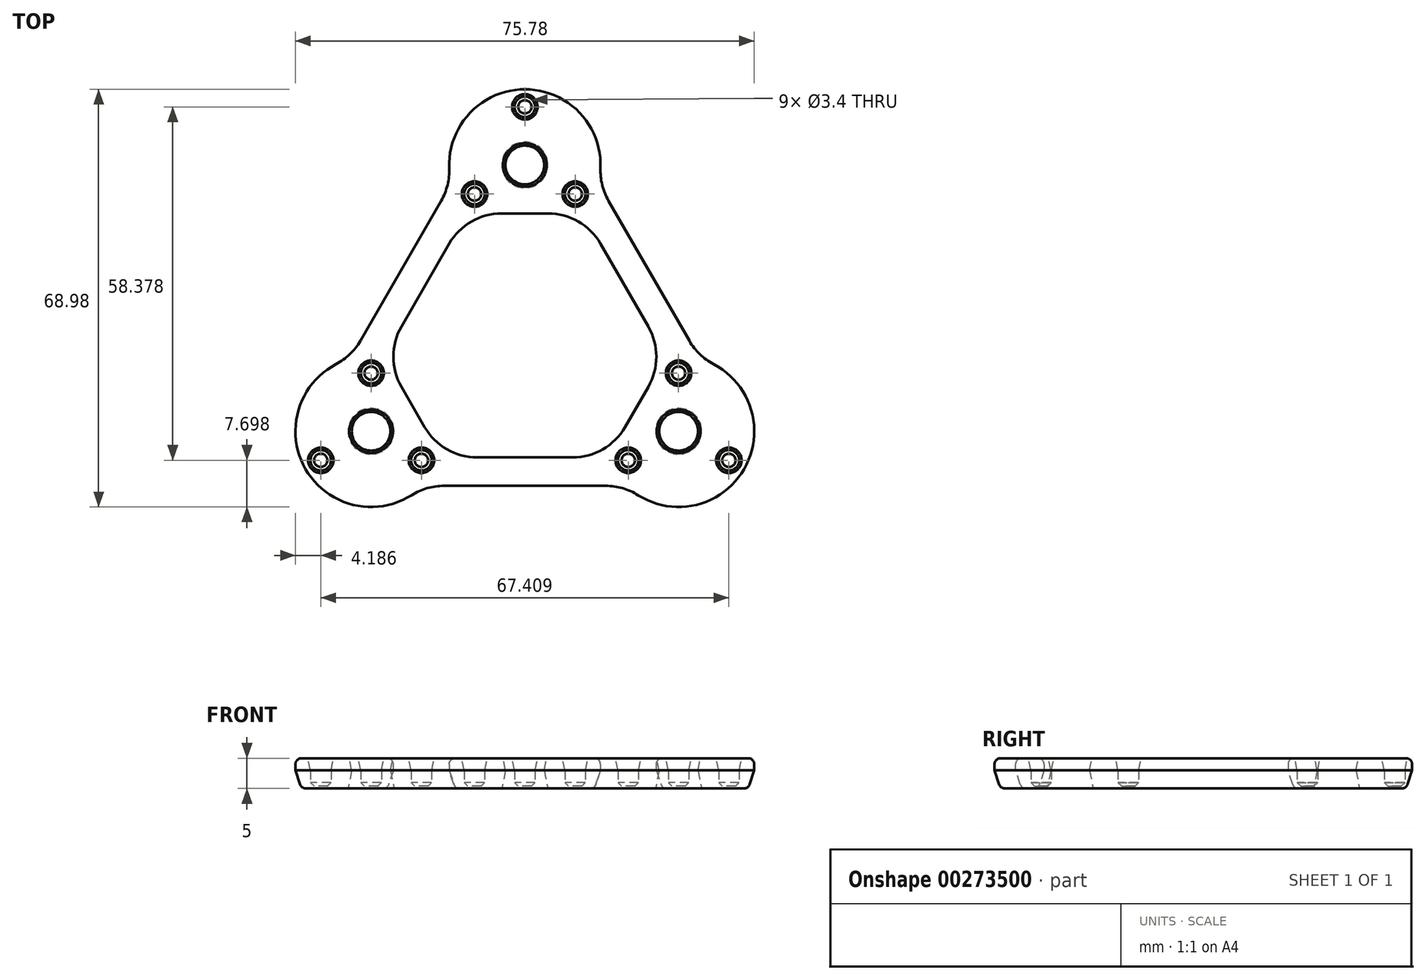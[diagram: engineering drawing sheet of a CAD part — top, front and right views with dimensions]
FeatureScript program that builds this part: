
annotation { "Feature Type Name" : "Feature", "Feature Type Description" : "" }
export const myFeature = defineFeature(function(context is Context, id is Id, definition is map)
    precondition{}
    {
        {
            var Q0;
            Q0=qCreatedBy(makeId("Top.planeOp"),FACE);
            var sketch = newSketch(context, id + "F0", { "sketchPlane" : qUnion([Q0])});
            skCircle(sketch, "E0", {"center": v(0, 29.45) * mm, "radius": 3.2 * mm});
            skCircle(sketch, "E1", {"center": v(0, 29.45) * mm, "radius": 12.5 * mm});
            skCircle(sketch, "E2", {"center": v(0, 39.05) * mm, "radius": 1.7 * mm});
            skCircle(sketch, "E3.1.0", {"center": v(-8.31, 24.65) * mm, "radius": 1.7 * mm});
            skCircle(sketch, "E3.2.0", {"center": v(8.31, 24.65) * mm, "radius": 1.7 * mm});
            skLineSegment(sketch, "E4", {"start": v(-9.6, 21.45) * mm, "end": v(9.6, 21.45) * mm});
            skLineSegment(sketch, "E5", {"start": v(12.13, 26.45) * mm, "end": v(-12.13, 26.45) * mm, "construction": true});
            skCircle(sketch, "E6.1.0", {"center": v(-25.4, -14.53) * mm, "radius": 12.5 * mm});
            skCircle(sketch, "E6.1.1", {"center": v(-17.08, -19.33) * mm, "radius": 1.7 * mm});
            skLineSegment(sketch, "E6.1.2", {"start": v(-13.66, -18.85) * mm, "end": v(-23.26, -2.21) * mm});
            skCircle(sketch, "E6.1.3", {"center": v(-25.4, -4.93) * mm, "radius": 1.7 * mm});
            skPoint(sketch, "E6.1.4", {"position": v(-25.4, -14.53) * mm});
            skLineSegment(sketch, "E6.1.5", {"start": v(-28.86, -2.52) * mm, "end": v(-16.73, -23.54) * mm, "construction": true});
            skCircle(sketch, "E6.1.6", {"center": v(-25.4, -14.53) * mm, "radius": 3.2 * mm});
            skCircle(sketch, "E6.1.7", {"center": v(-33.7, -19.33) * mm, "radius": 1.7 * mm});
            skCircle(sketch, "E6.2.0", {"center": v(25.4, -14.53) * mm, "radius": 12.5 * mm});
            skCircle(sketch, "E6.2.1", {"center": v(25.4, -4.93) * mm, "radius": 1.7 * mm});
            skLineSegment(sketch, "E6.2.2", {"start": v(23.26, -2.21) * mm, "end": v(13.66, -18.85) * mm});
            skCircle(sketch, "E6.2.3", {"center": v(17.08, -19.33) * mm, "radius": 1.7 * mm});
            skPoint(sketch, "E6.2.4", {"position": v(25.4, -14.53) * mm});
            skLineSegment(sketch, "E6.2.5", {"start": v(16.73, -23.54) * mm, "end": v(28.86, -2.52) * mm, "construction": true});
            skCircle(sketch, "E6.2.6", {"center": v(25.4, -14.53) * mm, "radius": 3.2 * mm});
            skCircle(sketch, "E6.2.7", {"center": v(33.7, -19.33) * mm, "radius": 1.7 * mm});
            skPoint(sketch, "E6.center", {"position": v(0, 0.13) * mm});
            skLineSegment(sketch, "E7", {"start": v(-23.26, -2.21) * mm, "end": v(-9.6, 21.45) * mm});
            skLineSegment(sketch, "E8", {"start": v(9.6, 21.45) * mm, "end": v(23.26, -2.21) * mm});
            skLineSegment(sketch, "E9", {"start": v(13.66, -18.85) * mm, "end": v(-13.66, -18.85) * mm});
            skLineSegment(sketch, "E10", {"start": v(-28.86, -2.52) * mm, "end": v(-12.13, 26.45) * mm});
            skLineSegment(sketch, "E11", {"start": v(12.13, 26.45) * mm, "end": v(28.86, -2.52) * mm});
            skLineSegment(sketch, "E12", {"start": v(-16.73, -23.54) * mm, "end": v(16.73, -23.54) * mm});
            skSolve(sketch);
        }
        {
            var Q0;
            Q0 = qSketchRegion(id + "F0", true);
            extrude(context, id + "F1", {"entities" : qUnion([Q0]), "depth" : 5 * mm, "offsetDistance" : 25 * mm});
        }
        {
            var Q0;
            Q0=makeQuery(id+"F0.imprint","IMPRINT",FACE,{"disambiguationData":[TD([[makeQuery(id+"F0.imprint","IMPRINT",EDGE,{"derivedFrom":sQuery(id+"F0.wireOp",EDGE,"E6.2.7")}),1.0]])]});
            var Q1;
            Q1=makeQuery(id+"F0.imprint","IMPRINT",FACE,{"disambiguationData":[TD([[makeQuery(id+"F0.imprint","IMPRINT",EDGE,{"derivedFrom":sQuery(id+"F0.wireOp",EDGE,"E6.2.1")}),1.0]])]});
            var Q2;
            Q2=makeQuery(id+"F0.imprint","IMPRINT",FACE,{"disambiguationData":[TD([[makeQuery(id+"F0.imprint","IMPRINT",EDGE,{"derivedFrom":sQuery(id+"F0.wireOp",EDGE,"E2")}),1.0]])]});
            var Q3;
            Q3=makeQuery(id+"F0.imprint","IMPRINT",FACE,{"disambiguationData":[TD([[makeQuery(id+"F0.imprint","IMPRINT",EDGE,{"derivedFrom":sQuery(id+"F0.wireOp",EDGE,"E6.1.3")}),1.0]])]});
            var Q4;
            Q4=makeQuery(id+"F0.imprint","IMPRINT",FACE,{"disambiguationData":[TD([[makeQuery(id+"F0.imprint","IMPRINT",EDGE,{"derivedFrom":sQuery(id+"F0.wireOp",EDGE,"E6.1.1")}),1.0]])]});
            var Q5;
            Q5=makeQuery(id+"F0.imprint","IMPRINT",FACE,{"disambiguationData":[TD([[makeQuery(id+"F0.imprint","IMPRINT",EDGE,{"derivedFrom":sQuery(id+"F0.wireOp",EDGE,"E6.1.7")}),1.0]])]});
            var Q6;
            Q6=makeQuery(id+"F0.imprint","IMPRINT",FACE,{"disambiguationData":[TD([[makeQuery(id+"F0.imprint","IMPRINT",EDGE,{"derivedFrom":sQuery(id+"F0.wireOp",EDGE,"E6.2.3")}),1.0]])]});
            var Q7;
            Q7=makeQuery(id+"F0.imprint","IMPRINT",FACE,{"disambiguationData":[TD([[makeQuery(id+"F0.imprint","IMPRINT",EDGE,{"derivedFrom":sQuery(id+"F0.wireOp",EDGE,"E3.2.0")}),1.0]])]});
            var Q8;
            Q8=makeQuery(id+"F0.imprint","IMPRINT",FACE,{"disambiguationData":[TD([[makeQuery(id+"F0.imprint","IMPRINT",EDGE,{"derivedFrom":sQuery(id+"F0.wireOp",EDGE,"E3.1.0")}),1.0]])]});
            extrude(context, id + "F2", {"entities" : qUnion([Q0, Q1, Q2, Q3, Q4, Q5, Q6, Q7, Q8]), "operationType" : NewBodyOperationType.ADD, "depth" : 0.4 * mm, "offsetDistance" : 25 * mm});
        }
        {
            var Q0;
            Q0=makeQuery(id+"F1.opExtrude","CAP_EDGE",EDGE,{"disambiguationData":[OSD([sQuery(id+"F0.wireOp",EDGE,"E6.1.6")])],"isStart":true});
            var Q1;
            Q1=makeQuery(id+"F1.opExtrude","CAP_EDGE",EDGE,{"disambiguationData":[OSD([sQuery(id+"F0.wireOp",EDGE,"E6.2.6")])],"isStart":true});
            var Q2;
            Q2=makeQuery(id+"F1.opExtrude","CAP_EDGE",EDGE,{"disambiguationData":[OSD([sQuery(id+"F0.wireOp",EDGE,"E0")])],"isStart":true});
            chamfer(context, id + "F3", {"entities" : qUnion([Q0, Q1, Q2]), "chamferType" : ChamferType.TWO_OFFSETS, "width1" : 0.6 * mm, "oppositeDirection" : false, "width2" : 3 * mm, "tangentPropagation" : true});
        }
        {
            var Q0;
            Q0=makeQuery(id+"F1.opExtrude","SWEPT_EDGE",EDGE,{"disambiguationData":[OSD([sQuery(id+"F0.wireOp",EDGE,"E1"),sQuery(id+"F0.wireOp",EDGE,"E4"),sQuery(id+"F0.wireOp",EDGE,"E7")])]});
            var Q1;
            Q1=makeQuery(id+"F1.opExtrude","SWEPT_EDGE",EDGE,{"disambiguationData":[OSD([sQuery(id+"F0.wireOp",EDGE,"E1"),sQuery(id+"F0.wireOp",EDGE,"E4"),sQuery(id+"F0.wireOp",EDGE,"E8")])]});
            var Q2;
            Q2=makeQuery(id+"F1.opExtrude","SWEPT_EDGE",EDGE,{"disambiguationData":[OSD([sQuery(id+"F0.wireOp",EDGE,"E6.1.0"),sQuery(id+"F0.wireOp",EDGE,"E6.1.2"),sQuery(id+"F0.wireOp",EDGE,"E7")])]});
            var Q3;
            Q3=makeQuery(id+"F1.opExtrude","SWEPT_EDGE",EDGE,{"disambiguationData":[OSD([sQuery(id+"F0.wireOp",EDGE,"E6.1.0"),sQuery(id+"F0.wireOp",EDGE,"E6.1.2"),sQuery(id+"F0.wireOp",EDGE,"E9")])]});
            var Q4;
            Q4=makeQuery(id+"F1.opExtrude","SWEPT_EDGE",EDGE,{"disambiguationData":[OSD([sQuery(id+"F0.wireOp",EDGE,"E6.2.0"),sQuery(id+"F0.wireOp",EDGE,"E6.2.2"),sQuery(id+"F0.wireOp",EDGE,"E9")])]});
            var Q5;
            Q5=makeQuery(id+"F1.opExtrude","SWEPT_EDGE",EDGE,{"disambiguationData":[OSD([sQuery(id+"F0.wireOp",EDGE,"E6.2.0"),sQuery(id+"F0.wireOp",EDGE,"E6.2.2"),sQuery(id+"F0.wireOp",EDGE,"E8")])]});
            var Q6;
            Q6=makeQuery(id+"F1.opExtrude","SWEPT_EDGE",EDGE,{"disambiguationData":[OSD([sQuery(id+"F0.wireOp",EDGE,"E6.2.0"),sQuery(id+"F0.wireOp",EDGE,"E12")])]});
            var Q7;
            Q7=makeQuery(id+"F1.opExtrude","SWEPT_EDGE",EDGE,{"disambiguationData":[OSD([sQuery(id+"F0.wireOp",EDGE,"E6.1.0"),sQuery(id+"F0.wireOp",EDGE,"E12")])]});
            var Q8;
            Q8=makeQuery(id+"F1.opExtrude","SWEPT_EDGE",EDGE,{"disambiguationData":[OSD([sQuery(id+"F0.wireOp",EDGE,"E6.1.0"),sQuery(id+"F0.wireOp",EDGE,"E10")])]});
            var Q9;
            Q9=makeQuery(id+"F1.opExtrude","SWEPT_EDGE",EDGE,{"disambiguationData":[OSD([sQuery(id+"F0.wireOp",EDGE,"E1"),sQuery(id+"F0.wireOp",EDGE,"E10")])]});
            var Q10;
            Q10=makeQuery(id+"F1.opExtrude","SWEPT_EDGE",EDGE,{"disambiguationData":[OSD([sQuery(id+"F0.wireOp",EDGE,"E1"),sQuery(id+"F0.wireOp",EDGE,"E11")])]});
            var Q11;
            Q11=makeQuery(id+"F1.opExtrude","SWEPT_EDGE",EDGE,{"disambiguationData":[OSD([sQuery(id+"F0.wireOp",EDGE,"E6.2.0"),sQuery(id+"F0.wireOp",EDGE,"E11")])]});
            fillet(context, id + "F4", {"entities" : qUnion([Q0, Q1, Q2, Q3, Q4, Q5, Q6, Q7, Q8, Q9, Q10, Q11]), "radius" : 10 * mm, "tangentPropagation" : true, "allowEdgeOverflow" : false});
        }
        {
            var Q0;
            Q0=makeQuery(id+"F1.opExtrude","CAP_EDGE",EDGE,{"disambiguationData":[OSD([sQuery(id+"F0.wireOp",EDGE,"E11")])],"isStart":true});
            var Q1;
            Q1=makeQuery(id+"F1.opExtrude","CAP_EDGE",EDGE,{"disambiguationData":[OSD([sQuery(id+"F0.wireOp",EDGE,"E8")])],"isStart":true});
            chamfer(context, id + "F5", {"entities" : qUnion([Q0, Q1]), "chamferType" : ChamferType.TWO_OFFSETS, "width1" : 1 * mm, "oppositeDirection" : false, "width2" : 3 * mm, "tangentPropagation" : true});
        }
        {
            var Q0;
            Q0=makeQuery(id+"F1.opExtrude","CAP_EDGE",EDGE,{"disambiguationData":[OSD([sQuery(id+"F0.wireOp",EDGE,"E9")])],"isStart":false});
            var Q1;
            Q1=makeQuery(id+"F1.opExtrude","CAP_EDGE",EDGE,{"disambiguationData":[OSD([sQuery(id+"F0.wireOp",EDGE,"E11")])],"isStart":false});
            fillet(context, id + "F6", {"entities" : qUnion([Q0, Q1]), "radius" : 1 * mm, "tangentPropagation" : true, "allowEdgeOverflow" : false});
        }
        {
            var Q0;
            Q0=makeQuery(id+"F1.opExtrude","CAP_EDGE",EDGE,{"disambiguationData":[OSD([sQuery(id+"F0.wireOp",EDGE,"E6.2.1")])],"isStart":false});
            var Q1;
            Q1=makeQuery(id+"F1.opExtrude","CAP_EDGE",EDGE,{"disambiguationData":[OSD([sQuery(id+"F0.wireOp",EDGE,"E6.2.3")])],"isStart":false});
            var Q2;
            Q2=makeQuery(id+"F1.opExtrude","CAP_EDGE",EDGE,{"disambiguationData":[OSD([sQuery(id+"F0.wireOp",EDGE,"E6.2.7")])],"isStart":false});
            var Q3;
            Q3=makeQuery(id+"F1.opExtrude","CAP_EDGE",EDGE,{"disambiguationData":[OSD([sQuery(id+"F0.wireOp",EDGE,"E6.1.7")])],"isStart":false});
            var Q4;
            Q4=makeQuery(id+"F1.opExtrude","CAP_EDGE",EDGE,{"disambiguationData":[OSD([sQuery(id+"F0.wireOp",EDGE,"E6.1.1")])],"isStart":false});
            var Q5;
            Q5=makeQuery(id+"F1.opExtrude","CAP_EDGE",EDGE,{"disambiguationData":[OSD([sQuery(id+"F0.wireOp",EDGE,"E6.1.3")])],"isStart":false});
            var Q6;
            Q6=makeQuery(id+"F1.opExtrude","CAP_EDGE",EDGE,{"disambiguationData":[OSD([sQuery(id+"F0.wireOp",EDGE,"E3.2.0")])],"isStart":false});
            var Q7;
            Q7=makeQuery(id+"F1.opExtrude","CAP_EDGE",EDGE,{"disambiguationData":[OSD([sQuery(id+"F0.wireOp",EDGE,"E3.1.0")])],"isStart":false});
            var Q8;
            Q8=makeQuery(id+"F1.opExtrude","CAP_EDGE",EDGE,{"disambiguationData":[OSD([sQuery(id+"F0.wireOp",EDGE,"E2")])],"isStart":false});
            var Q9;
            Q9=makeQuery(id+"F1.opExtrude","CAP_EDGE",EDGE,{"disambiguationData":[OSD([sQuery(id+"F0.wireOp",EDGE,"E6.2.6")])],"isStart":false});
            var Q10;
            Q10=makeQuery(id+"F1.opExtrude","CAP_EDGE",EDGE,{"disambiguationData":[OSD([sQuery(id+"F0.wireOp",EDGE,"E0")])],"isStart":false});
            var Q11;
            Q11=makeQuery(id+"F1.opExtrude","CAP_EDGE",EDGE,{"disambiguationData":[OSD([sQuery(id+"F0.wireOp",EDGE,"E6.1.6")])],"isStart":false});
            chamfer(context, id + "F7", {"entities" : qUnion([Q0, Q1, Q2, Q3, Q4, Q5, Q6, Q7, Q8, Q9, Q10, Q11]), "chamferType" : ChamferType.TWO_OFFSETS, "width1" : 0.4 * mm, "oppositeDirection" : true, "width2" : 2 * mm, "tangentPropagation" : true});
        }
        {
            var Q0;
            {var subQ0=sQuery(id+"F0.wireOp",EDGE,"E12");Q0=makeQuery(id+"F5.opChamfer","BLEND_EDGE",EDGE,{"blendedFrom":[makeQuery(id+"F1.opExtrude","CAP_EDGE",EDGE,{"disambiguationData":[OSD([subQ0])],"isStart":true}),makeQuery(id+"F1.opExtrude","CAP_FACE",FACE,{"disambiguationData":[OSD([sQuery(id+"F0.wireOp",EDGE,"E0"),sQuery(id+"F0.wireOp",EDGE,"E1"),sQuery(id+"F0.wireOp",EDGE,"E2"),sQuery(id+"F0.wireOp",EDGE,"E3.1.0"),sQuery(id+"F0.wireOp",EDGE,"E3.2.0"),sQuery(id+"F0.wireOp",EDGE,"E4"),sQuery(id+"F0.wireOp",EDGE,"E6.1.0"),sQuery(id+"F0.wireOp",EDGE,"E6.1.1"),sQuery(id+"F0.wireOp",EDGE,"E6.1.2"),sQuery(id+"F0.wireOp",EDGE,"E6.1.3"),sQuery(id+"F0.wireOp",EDGE,"E6.1.6"),sQuery(id+"F0.wireOp",EDGE,"E6.1.7"),sQuery(id+"F0.wireOp",EDGE,"E6.2.0"),sQuery(id+"F0.wireOp",EDGE,"E6.2.1"),sQuery(id+"F0.wireOp",EDGE,"E6.2.2"),sQuery(id+"F0.wireOp",EDGE,"E6.2.3"),sQuery(id+"F0.wireOp",EDGE,"E6.2.6"),sQuery(id+"F0.wireOp",EDGE,"E6.2.7"),sQuery(id+"F0.wireOp",EDGE,"E7"),sQuery(id+"F0.wireOp",EDGE,"E8"),sQuery(id+"F0.wireOp",EDGE,"E9"),sQuery(id+"F0.wireOp",EDGE,"E10"),sQuery(id+"F0.wireOp",EDGE,"E11"),subQ0])],"isStart":true})],"blendedInto":[makeQuery(id+"F1.opExtrude","CAP_FACE",FACE,{"disambiguationData":[OSD([sQuery(id+"F0.wireOp",EDGE,"E0"),sQuery(id+"F0.wireOp",EDGE,"E1"),sQuery(id+"F0.wireOp",EDGE,"E2"),sQuery(id+"F0.wireOp",EDGE,"E3.1.0"),sQuery(id+"F0.wireOp",EDGE,"E3.2.0"),sQuery(id+"F0.wireOp",EDGE,"E4"),sQuery(id+"F0.wireOp",EDGE,"E6.1.0"),sQuery(id+"F0.wireOp",EDGE,"E6.1.1"),sQuery(id+"F0.wireOp",EDGE,"E6.1.2"),sQuery(id+"F0.wireOp",EDGE,"E6.1.3"),sQuery(id+"F0.wireOp",EDGE,"E6.1.6"),sQuery(id+"F0.wireOp",EDGE,"E6.1.7"),sQuery(id+"F0.wireOp",EDGE,"E6.2.0"),sQuery(id+"F0.wireOp",EDGE,"E6.2.1"),sQuery(id+"F0.wireOp",EDGE,"E6.2.2"),sQuery(id+"F0.wireOp",EDGE,"E6.2.3"),sQuery(id+"F0.wireOp",EDGE,"E6.2.6"),sQuery(id+"F0.wireOp",EDGE,"E6.2.7"),sQuery(id+"F0.wireOp",EDGE,"E7"),sQuery(id+"F0.wireOp",EDGE,"E8"),sQuery(id+"F0.wireOp",EDGE,"E9"),sQuery(id+"F0.wireOp",EDGE,"E10"),sQuery(id+"F0.wireOp",EDGE,"E11"),subQ0])],"isStart":true})]});}
            var Q1;
            {var subQ0=sQuery(id+"F0.wireOp",EDGE,"E9");Q1=makeQuery(id+"F5.opChamfer","BLEND_EDGE",EDGE,{"blendedFrom":[makeQuery(id+"F1.opExtrude","CAP_EDGE",EDGE,{"disambiguationData":[OSD([subQ0])],"isStart":true}),makeQuery(id+"F1.opExtrude","CAP_FACE",FACE,{"disambiguationData":[OSD([sQuery(id+"F0.wireOp",EDGE,"E0"),sQuery(id+"F0.wireOp",EDGE,"E1"),sQuery(id+"F0.wireOp",EDGE,"E2"),sQuery(id+"F0.wireOp",EDGE,"E3.1.0"),sQuery(id+"F0.wireOp",EDGE,"E3.2.0"),sQuery(id+"F0.wireOp",EDGE,"E4"),sQuery(id+"F0.wireOp",EDGE,"E6.1.0"),sQuery(id+"F0.wireOp",EDGE,"E6.1.1"),sQuery(id+"F0.wireOp",EDGE,"E6.1.2"),sQuery(id+"F0.wireOp",EDGE,"E6.1.3"),sQuery(id+"F0.wireOp",EDGE,"E6.1.6"),sQuery(id+"F0.wireOp",EDGE,"E6.1.7"),sQuery(id+"F0.wireOp",EDGE,"E6.2.0"),sQuery(id+"F0.wireOp",EDGE,"E6.2.1"),sQuery(id+"F0.wireOp",EDGE,"E6.2.2"),sQuery(id+"F0.wireOp",EDGE,"E6.2.3"),sQuery(id+"F0.wireOp",EDGE,"E6.2.6"),sQuery(id+"F0.wireOp",EDGE,"E6.2.7"),sQuery(id+"F0.wireOp",EDGE,"E7"),sQuery(id+"F0.wireOp",EDGE,"E8"),subQ0,sQuery(id+"F0.wireOp",EDGE,"E10"),sQuery(id+"F0.wireOp",EDGE,"E11"),sQuery(id+"F0.wireOp",EDGE,"E12")])],"isStart":true})],"blendedInto":[makeQuery(id+"F1.opExtrude","CAP_FACE",FACE,{"disambiguationData":[OSD([sQuery(id+"F0.wireOp",EDGE,"E0"),sQuery(id+"F0.wireOp",EDGE,"E1"),sQuery(id+"F0.wireOp",EDGE,"E2"),sQuery(id+"F0.wireOp",EDGE,"E3.1.0"),sQuery(id+"F0.wireOp",EDGE,"E3.2.0"),sQuery(id+"F0.wireOp",EDGE,"E4"),sQuery(id+"F0.wireOp",EDGE,"E6.1.0"),sQuery(id+"F0.wireOp",EDGE,"E6.1.1"),sQuery(id+"F0.wireOp",EDGE,"E6.1.2"),sQuery(id+"F0.wireOp",EDGE,"E6.1.3"),sQuery(id+"F0.wireOp",EDGE,"E6.1.6"),sQuery(id+"F0.wireOp",EDGE,"E6.1.7"),sQuery(id+"F0.wireOp",EDGE,"E6.2.0"),sQuery(id+"F0.wireOp",EDGE,"E6.2.1"),sQuery(id+"F0.wireOp",EDGE,"E6.2.2"),sQuery(id+"F0.wireOp",EDGE,"E6.2.3"),sQuery(id+"F0.wireOp",EDGE,"E6.2.6"),sQuery(id+"F0.wireOp",EDGE,"E6.2.7"),sQuery(id+"F0.wireOp",EDGE,"E7"),sQuery(id+"F0.wireOp",EDGE,"E8"),subQ0,sQuery(id+"F0.wireOp",EDGE,"E10"),sQuery(id+"F0.wireOp",EDGE,"E11"),sQuery(id+"F0.wireOp",EDGE,"E12")])],"isStart":true})]});}
            fillet(context, id + "F8", {"entities" : qUnion([Q0, Q1]), "radius" : 1 * mm, "tangentPropagation" : true, "allowEdgeOverflow" : false});
        }
        {
            var Q0;
            Q0=makeQuery(id+"F2.opExtrude","CAP_FACE",FACE,{"disambiguationData":[OSD([sQuery(id+"F0.wireOp",EDGE,"E6.1.1")])],"isStart":false});
            var Q1;
            Q1=makeQuery(id+"F2.opExtrude","CAP_FACE",FACE,{"disambiguationData":[OSD([sQuery(id+"F0.wireOp",EDGE,"E6.1.3")])],"isStart":false});
            var Q2;
            Q2=makeQuery(id+"F2.opExtrude","CAP_FACE",FACE,{"disambiguationData":[OSD([sQuery(id+"F0.wireOp",EDGE,"E6.1.7")])],"isStart":false});
            var Q3;
            Q3=makeQuery(id+"F2.opExtrude","CAP_FACE",FACE,{"disambiguationData":[OSD([sQuery(id+"F0.wireOp",EDGE,"E6.2.7")])],"isStart":false});
            var Q4;
            Q4=makeQuery(id+"F2.opExtrude","CAP_FACE",FACE,{"disambiguationData":[OSD([sQuery(id+"F0.wireOp",EDGE,"E6.2.3")])],"isStart":false});
            var Q5;
            Q5=makeQuery(id+"F2.opExtrude","CAP_FACE",FACE,{"disambiguationData":[OSD([sQuery(id+"F0.wireOp",EDGE,"E6.2.1")])],"isStart":false});
            var Q6;
            Q6=makeQuery(id+"F2.opExtrude","CAP_FACE",FACE,{"disambiguationData":[OSD([sQuery(id+"F0.wireOp",EDGE,"E3.2.0")])],"isStart":false});
            var Q7;
            Q7=makeQuery(id+"F2.opExtrude","CAP_FACE",FACE,{"disambiguationData":[OSD([sQuery(id+"F0.wireOp",EDGE,"E3.1.0")])],"isStart":false});
            var Q8;
            Q8=makeQuery(id+"F2.opExtrude","CAP_FACE",FACE,{"disambiguationData":[OSD([sQuery(id+"F0.wireOp",EDGE,"E2")])],"isStart":false});
            chamfer(context, id + "F9", {"entities" : qUnion([Q0, Q1, Q2, Q3, Q4, Q5, Q6, Q7, Q8]), "width" : 0.6 * mm, "tangentPropagation" : true});
        }
    });
